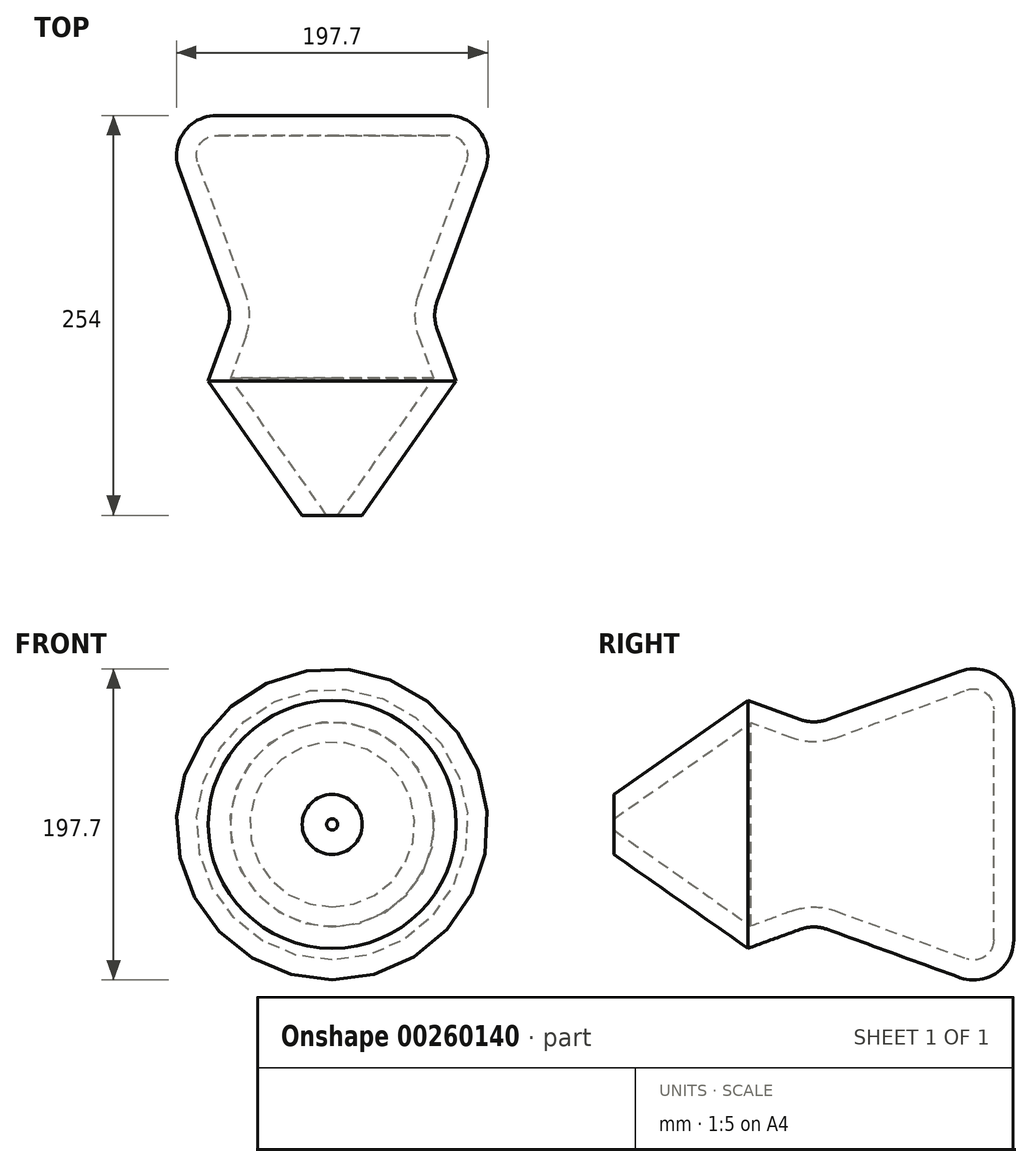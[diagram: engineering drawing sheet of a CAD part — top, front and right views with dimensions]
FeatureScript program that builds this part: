
annotation { "Feature Type Name" : "Feature", "Feature Type Description" : "" }
export const myFeature = defineFeature(function(context is Context, id is Id, definition is map)
    precondition{}
    {
        {
            var Q0;
            Q0=qCreatedBy(makeId("Front.planeOp"),FACE);
            var sketch = newSketch(context, id + "F0", { "sketchPlane" : qUnion([Q0])});
            skCircle(sketch, "E0", {"center": v(0, 0) * mm, "radius": 63.5 * mm});
            skSolve(sketch);
        }
        {
            var Q0;
            Q0 = qSketchRegion(id + "F0", true);
            extrude(context, id + "F1", {"entities" : qUnion([Q0]), "endBound" : BoundingType.SYMMETRIC, "depth" : 254 * mm, "hasDraft" : true, "draftAngle" : 20 * degree});
        }
        {
            var Q0;
            Q0=makeQuery(id+"F1.*.split.splitOp","SPLIT",FACE,{"derivedFrom":makeQuery(id+"F1.opExtrude","SWEPT_FACE",FACE,{"disambiguationData":[OSD([sQuery(id+"F0.wireOp",EDGE,"E0")])]}),"isFromBackBody":true});
            fillet(context, id + "F2", {"entities" : qUnion([Q0]), "radius" : 25.4 * mm, "tangentPropagation" : true, "allowEdgeOverflow" : false});
        }
        {
            var Q0;
            Q0=makeQuery(id+"F1.opExtrude","CAP_FACE",FACE,{"disambiguationData":[OSD([sQuery(id+"F0.wireOp",EDGE,"E0")])],"isStart":false});
            chamfer(context, id + "F3", {"entities" : qUnion([Q0]), "width" : 63.5 * mm, "tangentPropagation" : true});
        }
        {
            var Q0;
            Q0=makeQuery(id+"F1.opExtrude","CAP_FACE",FACE,{"disambiguationData":[OSD([sQuery(id+"F0.wireOp",EDGE,"E0")])],"isStart":false});
            shell(context, id + "F4", {"entities" : qUnion([Q0]), "thickness" : 12.7 * mm});
        }
    });
